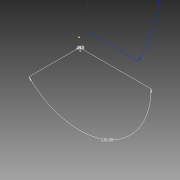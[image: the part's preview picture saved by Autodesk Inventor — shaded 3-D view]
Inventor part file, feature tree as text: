
AUTODESK INVENTOR PART (.ipt)
format: ipt  version: 2014 (Build 180170000, 170)  size: 93,184 bytes
history: native  units: in
note: dims shown in document units (in); Inventor stores cm internally (conversion verified against a paired STEP export)
features: sketch x1, reference x1, other x1, revolve x1
ambient origin geometry x8: Origin, YZ Plane, XZ Plane, XY Plane, X Axis, Y Axis, Z Axis, Center Point
bodies: Body1 (feature_tree)
feature tree (4):
  sketch  "Sketch1"  dims[d2=0.01in d3=0.01in d4=90.0deg]
  reference  "Reference1"
  other  "Srf1"
  revolve  "RevolutionSrf1"  [1 undecoded]
note: 1 required parameter value undecoded (feature->parameter linkage not recoverable at this tier; creation-order binding heuristic only, values carry confidence <= 0.55)
